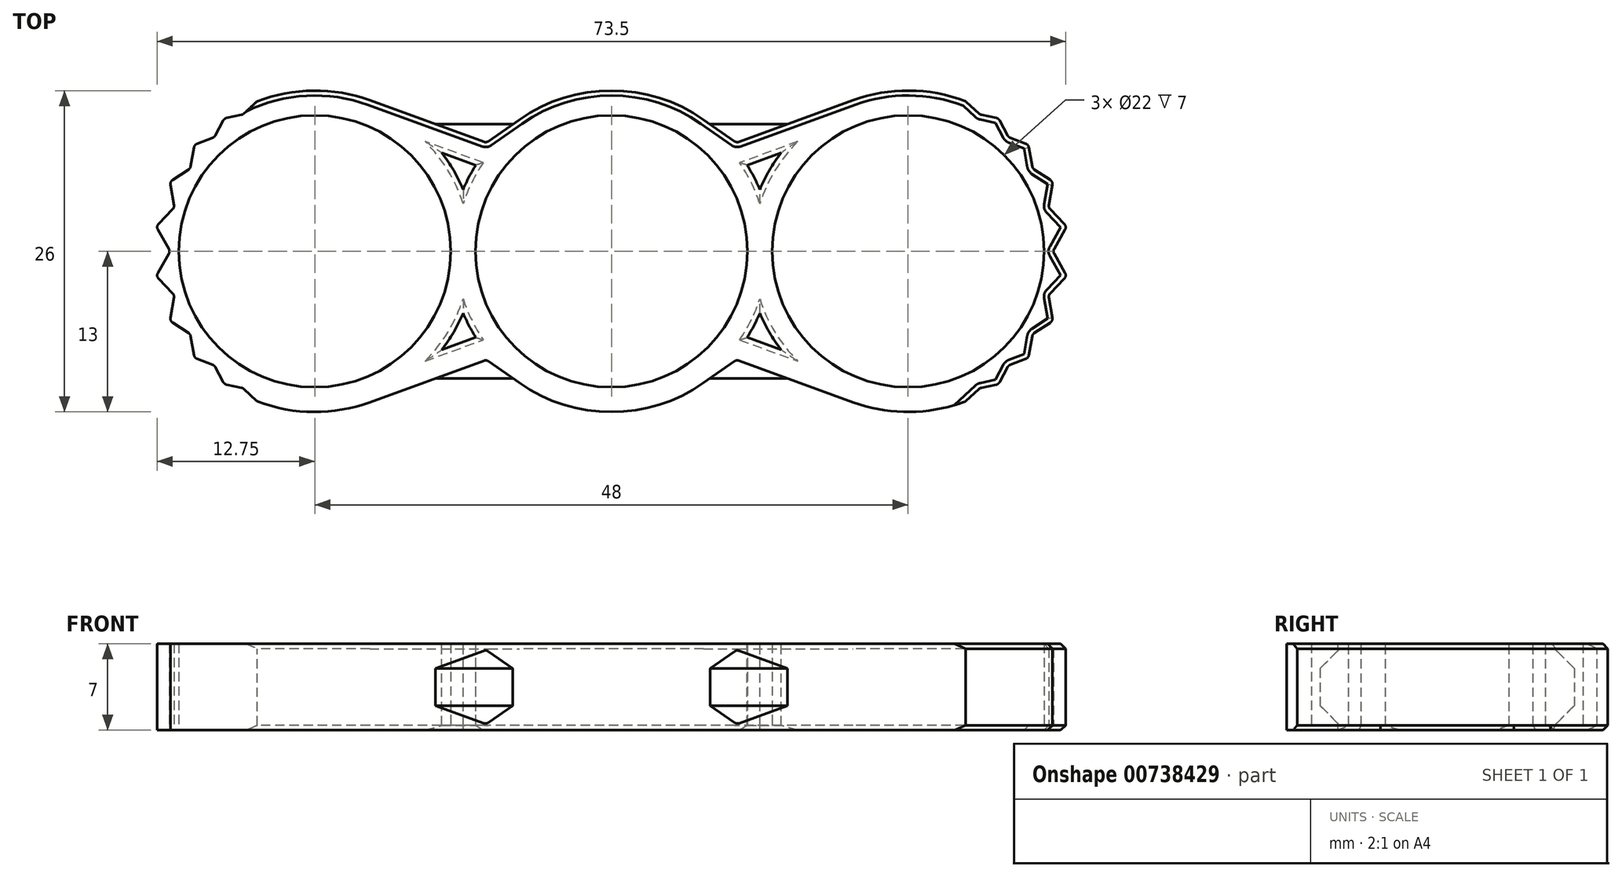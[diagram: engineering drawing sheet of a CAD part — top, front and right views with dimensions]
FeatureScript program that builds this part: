
annotation { "Feature Type Name" : "Feature", "Feature Type Description" : "" }
export const myFeature = defineFeature(function(context is Context, id is Id, definition is map)
    precondition{}
    {
        {
            var Q0;
            Q0=qCreatedBy(makeId("Top.planeOp"),FACE);
            var sketch = newSketch(context, id + "F0", { "sketchPlane" : qUnion([Q0])});
            skCircle(sketch, "E0", {"center": v(0, 0) * mm, "radius": 11 * mm});
            skCircle(sketch, "E1", {"center": v(0, 0) * mm, "radius": 13 * mm});
            skCircle(sketch, "E2", {"center": v(24, 0) * mm, "radius": 11 * mm});
            skCircle(sketch, "E3", {"center": v(-24, 0) * mm, "radius": 11 * mm});
            skLineSegment(sketch, "E4", {"start": v(-24, 0) * mm, "end": v(0, 0) * mm, "construction": true});
            skLineSegment(sketch, "E5", {"start": v(24, 0) * mm, "end": v(0, 0) * mm, "construction": true});
            skCircle(sketch, "E6", {"center": v(24, 0) * mm, "radius": 13 * mm});
            skCircle(sketch, "E7", {"center": v(-24, 0) * mm, "radius": 13 * mm});
            skLineSegment(sketch, "E8", {"start": v(-19.55, 12.22) * mm, "end": v(-10.12, 8.78) * mm});
            skLineSegment(sketch, "E9", {"start": v(-19.55, -12.22) * mm, "end": v(-10.12, -8.78) * mm});
            skLineSegment(sketch, "E10", {"start": v(19.55, -12.22) * mm, "end": v(10.12, -8.78) * mm});
            skLineSegment(sketch, "E11", {"start": v(19.55, 12.22) * mm, "end": v(10.12, 8.78) * mm});
            skLineSegment(sketch, "E12", {"start": v(-10.12, 8.78) * mm, "end": v(-7.46, 10.65) * mm});
            skLineSegment(sketch, "E13", {"start": v(7.46, 10.65) * mm, "end": v(10.12, 8.78) * mm});
            skLineSegment(sketch, "E14", {"start": v(10.12, -8.78) * mm, "end": v(7.46, -10.65) * mm});
            skLineSegment(sketch, "E15", {"start": v(-10.12, -8.78) * mm, "end": v(-7.46, -10.65) * mm});
            skLineSegment(sketch, "E16", {"start": v(10.12, 8.78) * mm, "end": v(10.12, -8.78) * mm, "construction": true});
            skLineSegment(sketch, "E17", {"start": v(-10.12, 8.78) * mm, "end": v(-10.12, -8.78) * mm, "construction": true});
            skSolve(sketch);
        }
        {
            var Q0;
            {var subQ4=sQuery(id+"F0.wireOp",EDGE,"E3");Q0=makeQuery(id+"F0.imprint","IMPRINT",FACE,{"disambiguationData":[TD([[makeQuery(id+"F0.imprint","IMPRINT",EDGE,{"derivedFrom":subQ4}),-1.0]])]});}
            var Q1;
            {var subQ3=sQuery(id+"F0.wireOp",EDGE,"E6");var subQ4=sQuery(id+"F0.wireOp",EDGE,"E0");var subQ5=makeQuery(id+"F0.imprint","INTERSECT",VERTEX,{"derivedFrom":[subQ4,subQ3]});Q1=makeQuery(id+"F0.imprint","IMPRINT",FACE,{"disambiguationData":[TD([[makeQuery(id+"F0.imprint","IMPRINT",EDGE,{"disambiguationData":[TD([[subQ5,-1.0]])],"derivedFrom":subQ4}),-1.0]])]});}
            var Q2;
            {var subQ0=sQuery(id+"F0.wireOp",EDGE,"E1");var subQ1=makeQuery(id+"F0.imprint","INTERSECT",VERTEX,{"derivedFrom":[subQ0,sQuery(id+"F0.wireOp",EDGE,"E3")]});Q2=makeQuery(id+"F0.imprint","IMPRINT",FACE,{"disambiguationData":[TD([[makeQuery(id+"F0.imprint","IMPRINT",EDGE,{"disambiguationData":[TD([[subQ1,1.0]])],"derivedFrom":subQ0}),1.0]])]});}
            var Q3;
            {var subQ2=sQuery(id+"F0.wireOp",EDGE,"E6");var subQ7=sQuery(id+"F0.wireOp",EDGE,"E0");var subQ8=makeQuery(id+"F0.imprint","INTERSECT",VERTEX,{"derivedFrom":[subQ7,subQ2]});Q3=makeQuery(id+"F0.imprint","IMPRINT",FACE,{"disambiguationData":[TD([[makeQuery(id+"F0.imprint","IMPRINT",EDGE,{"disambiguationData":[TD([[subQ8,1.0]])],"derivedFrom":subQ7}),-1.0]])]});}
            var Q4;
            {var subQ0=sQuery(id+"F0.wireOp",EDGE,"E1");var subQ1=makeQuery(id+"F0.imprint","INTERSECT",VERTEX,{"derivedFrom":[subQ0,sQuery(id+"F0.wireOp",EDGE,"E2")]});Q4=makeQuery(id+"F0.imprint","IMPRINT",FACE,{"disambiguationData":[TD([[makeQuery(id+"F0.imprint","IMPRINT",EDGE,{"disambiguationData":[TD([[subQ1,-1.0]])],"derivedFrom":subQ0}),1.0]])]});}
            var Q5;
            {var subQ4=sQuery(id+"F0.wireOp",EDGE,"E2");Q5=makeQuery(id+"F0.imprint","IMPRINT",FACE,{"disambiguationData":[TD([[makeQuery(id+"F0.imprint","IMPRINT",EDGE,{"derivedFrom":subQ4}),-1.0]])]});}
            var Q6;
            {var subQ4=sQuery(id+"F0.wireOp",EDGE,"E8");Q6=makeQuery(id+"F0.imprint","IMPRINT",FACE,{"disambiguationData":[TD([[makeQuery(id+"F0.imprint","IMPRINT",EDGE,{"derivedFrom":subQ4}),-1.0]])]});}
            var Q7;
            {var subQ4=sQuery(id+"F0.wireOp",EDGE,"E11");Q7=makeQuery(id+"F0.imprint","IMPRINT",FACE,{"disambiguationData":[TD([[makeQuery(id+"F0.imprint","IMPRINT",EDGE,{"derivedFrom":subQ4}),1.0]])]});}
            var Q8;
            {var subQ4=sQuery(id+"F0.wireOp",EDGE,"E9");Q8=makeQuery(id+"F0.imprint","IMPRINT",FACE,{"disambiguationData":[TD([[makeQuery(id+"F0.imprint","IMPRINT",EDGE,{"derivedFrom":subQ4}),1.0]])]});}
            var Q9;
            {var subQ4=sQuery(id+"F0.wireOp",EDGE,"E10");Q9=makeQuery(id+"F0.imprint","IMPRINT",FACE,{"disambiguationData":[TD([[makeQuery(id+"F0.imprint","IMPRINT",EDGE,{"derivedFrom":subQ4}),-1.0]])]});}
            extrude(context, id + "F1", {"entities" : qUnion([Q0, Q1, Q2, Q3, Q4, Q5, Q6, Q7, Q8, Q9]), "depth" : 3.5 * mm, "offsetDistance" : 25 * mm, "hasSecondDirection" : true, "secondDirectionOppositeDirection" : true, "secondDirectionDepth" : 3.5 * mm});
        }
        {
            var Q0;
            Q0=qCreatedBy(makeId("Top.planeOp"),FACE);
            var sketch = newSketch(context, id + "F2", { "sketchPlane" : qUnion([Q0])});
            skLineSegment(sketch, "E18", {"start": v(-14.24, -10.28) * mm, "end": v(-10.12, -8.78) * mm});
            skLineSegment(sketch, "E19", {"start": v(-10.12, -8.78) * mm, "end": v(-7.98, -10.28) * mm});
            skLineSegment(sketch, "E20", {"start": v(-7.98, -10.28) * mm, "end": v(-14.24, -10.28) * mm});
            skLineSegment(sketch, "E21", {"start": v(7.98, -10.28) * mm, "end": v(10.12, -8.78) * mm});
            skLineSegment(sketch, "E22", {"start": v(10.12, -8.78) * mm, "end": v(14.24, -10.28) * mm});
            skLineSegment(sketch, "E23", {"start": v(14.24, -10.28) * mm, "end": v(7.98, -10.28) * mm});
            skLineSegment(sketch, "E24", {"start": v(14.24, 10.28) * mm, "end": v(7.98, 10.28) * mm});
            skLineSegment(sketch, "E25", {"start": v(7.98, 10.28) * mm, "end": v(10.12, 8.78) * mm});
            skLineSegment(sketch, "E26", {"start": v(10.12, 8.78) * mm, "end": v(14.24, 10.28) * mm});
            skLineSegment(sketch, "E27", {"start": v(-7.98, 10.28) * mm, "end": v(-14.24, 10.28) * mm});
            skLineSegment(sketch, "E28", {"start": v(-14.24, 10.28) * mm, "end": v(-10.12, 8.78) * mm});
            skLineSegment(sketch, "E29", {"start": v(-10.12, 8.78) * mm, "end": v(-7.98, 10.28) * mm});
            skSolve(sketch);
        }
        {
            var Q0;
            Q0 = qSketchRegion(id + "F2", true);
            extrude(context, id + "F3", {"entities" : qUnion([Q0]), "operationType" : NewBodyOperationType.ADD, "depth" : 3 * mm, "offsetDistance" : 25 * mm, "hasSecondDirection" : true, "secondDirectionOppositeDirection" : true, "secondDirectionDepth" : 3 * mm});
        }
        {
            var Q0;
            Q0=makeQuery(id+"F3.opExtrude","CAP_EDGE",EDGE,{"disambiguationData":[OSD([sQuery(id+"F2.wireOp",EDGE,"E20")])],"isStart":false});
            var Q1;
            Q1=makeQuery(id+"F3.opExtrude","CAP_EDGE",EDGE,{"disambiguationData":[OSD([sQuery(id+"F2.wireOp",EDGE,"E20")])],"isStart":true});
            var Q2;
            Q2=makeQuery(id+"F3.opExtrude","CAP_EDGE",EDGE,{"disambiguationData":[OSD([sQuery(id+"F2.wireOp",EDGE,"E23")])],"isStart":true});
            var Q3;
            Q3=makeQuery(id+"F3.opExtrude","CAP_EDGE",EDGE,{"disambiguationData":[OSD([sQuery(id+"F2.wireOp",EDGE,"E23")])],"isStart":false});
            var Q4;
            Q4=makeQuery(id+"F3.opExtrude","CAP_EDGE",EDGE,{"disambiguationData":[OSD([sQuery(id+"F2.wireOp",EDGE,"E24")])],"isStart":false});
            var Q5;
            Q5=makeQuery(id+"F3.opExtrude","CAP_EDGE",EDGE,{"disambiguationData":[OSD([sQuery(id+"F2.wireOp",EDGE,"E27")])],"isStart":false});
            var Q6;
            Q6=makeQuery(id+"F3.opExtrude","CAP_EDGE",EDGE,{"disambiguationData":[OSD([sQuery(id+"F2.wireOp",EDGE,"E24")])],"isStart":true});
            var Q7;
            Q7=makeQuery(id+"F3.opExtrude","CAP_EDGE",EDGE,{"disambiguationData":[OSD([sQuery(id+"F2.wireOp",EDGE,"E27")])],"isStart":true});
            chamfer(context, id + "F4", {"entities" : qUnion([Q0, Q1, Q2, Q3, Q4, Q5, Q6, Q7]), "width" : 1.5 * mm, "tangentPropagation" : true});
        }
        {
            var Q0;
            Q0=qCreatedBy(makeId("Top.planeOp"),FACE);
            var sketch = newSketch(context, id + "F5", { "sketchPlane" : qUnion([Q0])});
            skLineSegment(sketch, "E30", {"start": v(35.7, 0) * mm, "end": v(36.85, 2) * mm});
            skLineSegment(sketch, "E31", {"start": v(36.85, -2) * mm, "end": v(35.7, 0) * mm});
            skLineSegment(sketch, "E32", {"start": v(35.7, 0) * mm, "end": v(24, 0) * mm, "construction": true});
            skLineSegment(sketch, "E33", {"start": v(36.85, 2) * mm, "end": v(35.36, 3.53) * mm});
            skLineSegment(sketch, "E34", {"start": v(35.36, 3.53) * mm, "end": v(35.72, 5.63) * mm});
            skLineSegment(sketch, "E35", {"start": v(35.36, 3.53) * mm, "end": v(24, 0) * mm, "construction": true});
            skLineSegment(sketch, "E36", {"start": v(35.72, 5.63) * mm, "end": v(34.08, 6.7) * mm});
            skLineSegment(sketch, "E37", {"start": v(34.08, 6.7) * mm, "end": v(33.73, 8.63) * mm});
            skLineSegment(sketch, "E38", {"start": v(34.08, 6.7) * mm, "end": v(24, 0) * mm, "construction": true});
            skLineSegment(sketch, "E39.MirrorCS", {"start": v(36.85, -2) * mm, "end": v(35.36, -3.53) * mm});
            skLineSegment(sketch, "E40.MirrorCS", {"start": v(35.36, -3.53) * mm, "end": v(24, 0) * mm, "construction": true});
            skLineSegment(sketch, "E41.MirrorCS", {"start": v(35.36, -3.53) * mm, "end": v(35.72, -5.63) * mm});
            skLineSegment(sketch, "E42.MirrorCS", {"start": v(35.72, -5.63) * mm, "end": v(34.08, -6.7) * mm});
            skLineSegment(sketch, "E43.MirrorCS", {"start": v(34.08, -6.7) * mm, "end": v(24, 0) * mm, "construction": true});
            skLineSegment(sketch, "E44.MirrorCS", {"start": v(34.08, -6.7) * mm, "end": v(33.73, -8.63) * mm});
            skLineSegment(sketch, "E45", {"start": v(39.5, 12.13) * mm, "end": v(39.5, -12.13) * mm});
            skLineSegment(sketch, "E46", {"start": v(33.73, 8.63) * mm, "end": v(32.13, 9.23) * mm});
            skLineSegment(sketch, "E47", {"start": v(32.13, 9.23) * mm, "end": v(31.32, 10.74) * mm});
            skLineSegment(sketch, "E48", {"start": v(32.13, 9.23) * mm, "end": v(24, 0) * mm, "construction": true});
            skLineSegment(sketch, "E49.MirrorCS", {"start": v(32.13, -9.23) * mm, "end": v(24, 0) * mm, "construction": true});
            skLineSegment(sketch, "E50.MirrorCS", {"start": v(32.13, -9.23) * mm, "end": v(31.32, -10.74) * mm});
            skLineSegment(sketch, "E51.MirrorCS", {"start": v(33.73, -8.63) * mm, "end": v(32.13, -9.23) * mm});
            skLineSegment(sketch, "E52", {"start": v(31.32, 10.74) * mm, "end": v(29.8, 11.07) * mm});
            skLineSegment(sketch, "E53", {"start": v(29.8, 11.07) * mm, "end": v(28.67, 12.13) * mm});
            skLineSegment(sketch, "E54", {"start": v(29.8, 11.07) * mm, "end": v(24, 0) * mm, "construction": true});
            skLineSegment(sketch, "E55", {"start": v(28.67, 12.13) * mm, "end": v(39.5, 12.13) * mm});
            skLineSegment(sketch, "E56.MirrorCS", {"start": v(29.8, -11.07) * mm, "end": v(24, 0) * mm, "construction": true});
            skLineSegment(sketch, "E57.MirrorCS", {"start": v(31.32, -10.74) * mm, "end": v(29.8, -11.07) * mm});
            skLineSegment(sketch, "E58.MirrorCS", {"start": v(29.8, -11.07) * mm, "end": v(28.67, -12.13) * mm});
            skLineSegment(sketch, "E59", {"start": v(28.67, -12.13) * mm, "end": v(39.5, -12.13) * mm});
            skLineSegment(sketch, "E60", {"start": v(0, 0) * mm, "end": v(0, 11) * mm, "construction": true});
            skLineSegment(sketch, "E61.MirrorCS", {"start": v(-29.8, 11.07) * mm, "end": v(-28.67, 12.13) * mm});
            skLineSegment(sketch, "E62.MirrorCS", {"start": v(-29.8, -11.07) * mm, "end": v(-28.67, -12.13) * mm});
            skLineSegment(sketch, "E63.MirrorCS", {"start": v(-31.32, -10.74) * mm, "end": v(-29.8, -11.07) * mm});
            skLineSegment(sketch, "E64.MirrorCS", {"start": v(-32.13, -9.23) * mm, "end": v(-31.32, -10.74) * mm});
            skLineSegment(sketch, "E65.MirrorCS", {"start": v(-31.32, 10.74) * mm, "end": v(-29.8, 11.07) * mm});
            skLineSegment(sketch, "E66.MirrorCS", {"start": v(-34.08, 6.7) * mm, "end": v(-33.73, 8.63) * mm});
            skLineSegment(sketch, "E67.MirrorCS", {"start": v(-34.08, -6.7) * mm, "end": v(-33.73, -8.63) * mm});
            skLineSegment(sketch, "E68.MirrorCS", {"start": v(-35.72, 5.63) * mm, "end": v(-34.08, 6.7) * mm});
            skLineSegment(sketch, "E69.MirrorCS", {"start": v(-33.73, 8.63) * mm, "end": v(-32.13, 9.23) * mm});
            skLineSegment(sketch, "E70.MirrorCS", {"start": v(-32.13, 9.23) * mm, "end": v(-31.32, 10.74) * mm});
            skLineSegment(sketch, "E71.MirrorCS", {"start": v(-33.73, -8.63) * mm, "end": v(-32.13, -9.23) * mm});
            skLineSegment(sketch, "E72.MirrorCS", {"start": v(-36.85, 2) * mm, "end": v(-35.36, 3.53) * mm});
            skLineSegment(sketch, "E73.MirrorCS", {"start": v(-35.72, -5.63) * mm, "end": v(-34.08, -6.7) * mm});
            skLineSegment(sketch, "E74.MirrorCS", {"start": v(-36.85, -2) * mm, "end": v(-35.7, 0) * mm});
            skLineSegment(sketch, "E75.MirrorCS", {"start": v(-32.13, 9.23) * mm, "end": v(-24, 0) * mm, "construction": true});
            skLineSegment(sketch, "E76.MirrorCS", {"start": v(-35.7, 0) * mm, "end": v(-36.85, 2) * mm});
            skLineSegment(sketch, "E77.MirrorCS", {"start": v(-35.36, -3.53) * mm, "end": v(-35.72, -5.63) * mm});
            skLineSegment(sketch, "E78.MirrorCS", {"start": v(-28.67, 12.13) * mm, "end": v(-39.5, 12.13) * mm});
            skLineSegment(sketch, "E79.MirrorCS", {"start": v(-34.08, -6.7) * mm, "end": v(-24, 0) * mm, "construction": true});
            skLineSegment(sketch, "E80.MirrorCS", {"start": v(-29.8, -11.07) * mm, "end": v(-24, 0) * mm, "construction": true});
            skLineSegment(sketch, "E81.MirrorCS", {"start": v(-36.85, -2) * mm, "end": v(-35.36, -3.53) * mm});
            skLineSegment(sketch, "E82.MirrorCS", {"start": v(-35.36, 3.53) * mm, "end": v(-24, 0) * mm, "construction": true});
            skLineSegment(sketch, "E83.MirrorCS", {"start": v(-35.7, 0) * mm, "end": v(-24, 0) * mm, "construction": true});
            skLineSegment(sketch, "E84.MirrorCS", {"start": v(-35.36, 3.53) * mm, "end": v(-35.72, 5.63) * mm});
            skLineSegment(sketch, "E85.MirrorCS", {"start": v(-28.67, -12.13) * mm, "end": v(-39.5, -12.13) * mm});
            skLineSegment(sketch, "E86.MirrorCS", {"start": v(-29.8, 11.07) * mm, "end": v(-24, 0) * mm, "construction": true});
            skLineSegment(sketch, "E87.MirrorCS", {"start": v(-34.08, 6.7) * mm, "end": v(-24, 0) * mm, "construction": true});
            skLineSegment(sketch, "E88.MirrorCS", {"start": v(-32.13, -9.23) * mm, "end": v(-24, 0) * mm, "construction": true});
            skLineSegment(sketch, "E89.MirrorCS", {"start": v(-35.36, -3.53) * mm, "end": v(-24, 0) * mm, "construction": true});
            skLineSegment(sketch, "E90.MirrorCS", {"start": v(-39.5, 12.13) * mm, "end": v(-39.5, -12.13) * mm});
            skSolve(sketch);
        }
        {
            var Q0;
            Q0 = qSketchRegion(id + "F5", true);
            extrude(context, id + "F6", {"entities" : qUnion([Q0]), "operationType" : NewBodyOperationType.REMOVE, "endBound" : BoundingType.THROUGH_ALL, "oppositeDirection" : true, "depth" : 25 * mm, "offsetDistance" : 25 * mm, "hasSecondDirection" : true, "secondDirectionBound" : SecondDirectionBoundingType.THROUGH_ALL, "secondDirectionOppositeDirection" : false, "secondDirectionDepth" : 25 * mm});
        }
        {
            var Q0;
            Q0=makeQuery(id+"F6.boolean.opBoolean","COPY",EDGE,{"derivedFrom":makeQuery(id+"F6.opExtrude","SWEPT_EDGE",EDGE,{"disambiguationData":[OSD([sQuery(id+"F5.wireOp",EDGE,"E61.MirrorCS"),sQuery(id+"F5.wireOp",EDGE,"E78.MirrorCS")])]})});
            var Q1;
            Q1=makeQuery(id+"F6.boolean.opBoolean","COPY",EDGE,{"derivedFrom":makeQuery(id+"F6.opExtrude","SWEPT_EDGE",EDGE,{"disambiguationData":[OSD([sQuery(id+"F5.wireOp",EDGE,"E61.MirrorCS"),sQuery(id+"F5.wireOp",EDGE,"E65.MirrorCS")])]})});
            var Q2;
            Q2=makeQuery(id+"F6.boolean.opBoolean","COPY",EDGE,{"derivedFrom":makeQuery(id+"F6.opExtrude","SWEPT_EDGE",EDGE,{"disambiguationData":[OSD([sQuery(id+"F5.wireOp",EDGE,"E65.MirrorCS"),sQuery(id+"F5.wireOp",EDGE,"E70.MirrorCS")])]})});
            var Q3;
            Q3=makeQuery(id+"F6.boolean.opBoolean","COPY",EDGE,{"derivedFrom":makeQuery(id+"F6.opExtrude","SWEPT_EDGE",EDGE,{"disambiguationData":[OSD([sQuery(id+"F5.wireOp",EDGE,"E69.MirrorCS"),sQuery(id+"F5.wireOp",EDGE,"E70.MirrorCS")])]})});
            var Q4;
            Q4=makeQuery(id+"F6.boolean.opBoolean","COPY",EDGE,{"derivedFrom":makeQuery(id+"F6.opExtrude","SWEPT_EDGE",EDGE,{"disambiguationData":[OSD([sQuery(id+"F5.wireOp",EDGE,"E66.MirrorCS"),sQuery(id+"F5.wireOp",EDGE,"E69.MirrorCS")])]})});
            var Q5;
            Q5=makeQuery(id+"F6.boolean.opBoolean","COPY",EDGE,{"derivedFrom":makeQuery(id+"F6.opExtrude","SWEPT_EDGE",EDGE,{"disambiguationData":[OSD([sQuery(id+"F5.wireOp",EDGE,"E66.MirrorCS"),sQuery(id+"F5.wireOp",EDGE,"E68.MirrorCS")])]})});
            var Q6;
            Q6=makeQuery(id+"F6.boolean.opBoolean","COPY",EDGE,{"derivedFrom":makeQuery(id+"F6.opExtrude","SWEPT_EDGE",EDGE,{"disambiguationData":[OSD([sQuery(id+"F5.wireOp",EDGE,"E68.MirrorCS"),sQuery(id+"F5.wireOp",EDGE,"E84.MirrorCS")])]})});
            var Q7;
            Q7=makeQuery(id+"F6.boolean.opBoolean","COPY",EDGE,{"derivedFrom":makeQuery(id+"F6.opExtrude","SWEPT_EDGE",EDGE,{"disambiguationData":[OSD([sQuery(id+"F5.wireOp",EDGE,"E72.MirrorCS"),sQuery(id+"F5.wireOp",EDGE,"E84.MirrorCS")])]})});
            var Q8;
            Q8=makeQuery(id+"F6.boolean.opBoolean","COPY",EDGE,{"derivedFrom":makeQuery(id+"F6.opExtrude","SWEPT_EDGE",EDGE,{"disambiguationData":[OSD([sQuery(id+"F5.wireOp",EDGE,"E72.MirrorCS"),sQuery(id+"F5.wireOp",EDGE,"E76.MirrorCS")])]})});
            var Q9;
            Q9=makeQuery(id+"F6.boolean.opBoolean","COPY",EDGE,{"derivedFrom":makeQuery(id+"F6.opExtrude","SWEPT_EDGE",EDGE,{"disambiguationData":[OSD([sQuery(id+"F5.wireOp",EDGE,"E74.MirrorCS"),sQuery(id+"F5.wireOp",EDGE,"E76.MirrorCS")])]})});
            var Q10;
            Q10=makeQuery(id+"F6.boolean.opBoolean","COPY",EDGE,{"derivedFrom":makeQuery(id+"F6.opExtrude","SWEPT_EDGE",EDGE,{"disambiguationData":[OSD([sQuery(id+"F5.wireOp",EDGE,"E74.MirrorCS"),sQuery(id+"F5.wireOp",EDGE,"E81.MirrorCS")])]})});
            var Q11;
            Q11=makeQuery(id+"F6.boolean.opBoolean","COPY",EDGE,{"derivedFrom":makeQuery(id+"F6.opExtrude","SWEPT_EDGE",EDGE,{"disambiguationData":[OSD([sQuery(id+"F5.wireOp",EDGE,"E77.MirrorCS"),sQuery(id+"F5.wireOp",EDGE,"E81.MirrorCS")])]})});
            var Q12;
            Q12=makeQuery(id+"F6.boolean.opBoolean","COPY",EDGE,{"derivedFrom":makeQuery(id+"F6.opExtrude","SWEPT_EDGE",EDGE,{"disambiguationData":[OSD([sQuery(id+"F5.wireOp",EDGE,"E73.MirrorCS"),sQuery(id+"F5.wireOp",EDGE,"E77.MirrorCS")])]})});
            var Q13;
            Q13=makeQuery(id+"F6.boolean.opBoolean","COPY",EDGE,{"derivedFrom":makeQuery(id+"F6.opExtrude","SWEPT_EDGE",EDGE,{"disambiguationData":[OSD([sQuery(id+"F5.wireOp",EDGE,"E67.MirrorCS"),sQuery(id+"F5.wireOp",EDGE,"E73.MirrorCS")])]})});
            var Q14;
            Q14=makeQuery(id+"F6.boolean.opBoolean","COPY",EDGE,{"derivedFrom":makeQuery(id+"F6.opExtrude","SWEPT_EDGE",EDGE,{"disambiguationData":[OSD([sQuery(id+"F5.wireOp",EDGE,"E67.MirrorCS"),sQuery(id+"F5.wireOp",EDGE,"E71.MirrorCS")])]})});
            var Q15;
            Q15=makeQuery(id+"F6.boolean.opBoolean","COPY",EDGE,{"derivedFrom":makeQuery(id+"F6.opExtrude","SWEPT_EDGE",EDGE,{"disambiguationData":[OSD([sQuery(id+"F5.wireOp",EDGE,"E64.MirrorCS"),sQuery(id+"F5.wireOp",EDGE,"E71.MirrorCS")])]})});
            var Q16;
            Q16=makeQuery(id+"F6.boolean.opBoolean","COPY",EDGE,{"derivedFrom":makeQuery(id+"F6.opExtrude","SWEPT_EDGE",EDGE,{"disambiguationData":[OSD([sQuery(id+"F5.wireOp",EDGE,"E63.MirrorCS"),sQuery(id+"F5.wireOp",EDGE,"E64.MirrorCS")])]})});
            var Q17;
            Q17=makeQuery(id+"F6.boolean.opBoolean","COPY",EDGE,{"derivedFrom":makeQuery(id+"F6.opExtrude","SWEPT_EDGE",EDGE,{"disambiguationData":[OSD([sQuery(id+"F5.wireOp",EDGE,"E62.MirrorCS"),sQuery(id+"F5.wireOp",EDGE,"E63.MirrorCS")])]})});
            var Q18;
            Q18=makeQuery(id+"F6.boolean.opBoolean","COPY",EDGE,{"derivedFrom":makeQuery(id+"F6.opExtrude","SWEPT_EDGE",EDGE,{"disambiguationData":[OSD([sQuery(id+"F5.wireOp",EDGE,"E62.MirrorCS"),sQuery(id+"F5.wireOp",EDGE,"E85.MirrorCS")])]})});
            var Q19;
            Q19=makeQuery(id+"F6.boolean.opBoolean","COPY",EDGE,{"derivedFrom":makeQuery(id+"F6.opExtrude","SWEPT_EDGE",EDGE,{"disambiguationData":[OSD([sQuery(id+"F5.wireOp",EDGE,"E58.MirrorCS"),sQuery(id+"F5.wireOp",EDGE,"E59")])]})});
            var Q20;
            Q20=makeQuery(id+"F6.boolean.opBoolean","COPY",EDGE,{"derivedFrom":makeQuery(id+"F6.opExtrude","SWEPT_EDGE",EDGE,{"disambiguationData":[OSD([sQuery(id+"F5.wireOp",EDGE,"E57.MirrorCS"),sQuery(id+"F5.wireOp",EDGE,"E58.MirrorCS")])]})});
            var Q21;
            Q21=makeQuery(id+"F6.boolean.opBoolean","COPY",EDGE,{"derivedFrom":makeQuery(id+"F6.opExtrude","SWEPT_EDGE",EDGE,{"disambiguationData":[OSD([sQuery(id+"F5.wireOp",EDGE,"E50.MirrorCS"),sQuery(id+"F5.wireOp",EDGE,"E57.MirrorCS")])]})});
            var Q22;
            Q22=makeQuery(id+"F6.boolean.opBoolean","COPY",EDGE,{"derivedFrom":makeQuery(id+"F6.opExtrude","SWEPT_EDGE",EDGE,{"disambiguationData":[OSD([sQuery(id+"F5.wireOp",EDGE,"E50.MirrorCS"),sQuery(id+"F5.wireOp",EDGE,"E51.MirrorCS")])]})});
            var Q23;
            Q23=makeQuery(id+"F6.boolean.opBoolean","COPY",EDGE,{"derivedFrom":makeQuery(id+"F6.opExtrude","SWEPT_EDGE",EDGE,{"disambiguationData":[OSD([sQuery(id+"F5.wireOp",EDGE,"E44.MirrorCS"),sQuery(id+"F5.wireOp",EDGE,"E51.MirrorCS")])]})});
            var Q24;
            Q24=makeQuery(id+"F6.boolean.opBoolean","COPY",EDGE,{"derivedFrom":makeQuery(id+"F6.opExtrude","SWEPT_EDGE",EDGE,{"disambiguationData":[OSD([sQuery(id+"F5.wireOp",EDGE,"E42.MirrorCS"),sQuery(id+"F5.wireOp",EDGE,"E44.MirrorCS")])]})});
            var Q25;
            Q25=makeQuery(id+"F6.boolean.opBoolean","COPY",EDGE,{"derivedFrom":makeQuery(id+"F6.opExtrude","SWEPT_EDGE",EDGE,{"disambiguationData":[OSD([sQuery(id+"F5.wireOp",EDGE,"E41.MirrorCS"),sQuery(id+"F5.wireOp",EDGE,"E42.MirrorCS")])]})});
            var Q26;
            Q26=makeQuery(id+"F6.boolean.opBoolean","COPY",EDGE,{"derivedFrom":makeQuery(id+"F6.opExtrude","SWEPT_EDGE",EDGE,{"disambiguationData":[OSD([sQuery(id+"F5.wireOp",EDGE,"E39.MirrorCS"),sQuery(id+"F5.wireOp",EDGE,"E41.MirrorCS")])]})});
            var Q27;
            Q27=makeQuery(id+"F6.boolean.opBoolean","COPY",EDGE,{"derivedFrom":makeQuery(id+"F6.opExtrude","SWEPT_EDGE",EDGE,{"disambiguationData":[OSD([sQuery(id+"F5.wireOp",EDGE,"E31"),sQuery(id+"F5.wireOp",EDGE,"E39.MirrorCS")])]})});
            var Q28;
            Q28=makeQuery(id+"F6.boolean.opBoolean","COPY",EDGE,{"derivedFrom":makeQuery(id+"F6.opExtrude","SWEPT_EDGE",EDGE,{"disambiguationData":[OSD([sQuery(id+"F5.wireOp",EDGE,"E30"),sQuery(id+"F5.wireOp",EDGE,"E31")])]})});
            var Q29;
            Q29=makeQuery(id+"F6.boolean.opBoolean","COPY",EDGE,{"derivedFrom":makeQuery(id+"F6.opExtrude","SWEPT_EDGE",EDGE,{"disambiguationData":[OSD([sQuery(id+"F5.wireOp",EDGE,"E30"),sQuery(id+"F5.wireOp",EDGE,"E33")])]})});
            var Q30;
            Q30=makeQuery(id+"F6.boolean.opBoolean","COPY",EDGE,{"derivedFrom":makeQuery(id+"F6.opExtrude","SWEPT_EDGE",EDGE,{"disambiguationData":[OSD([sQuery(id+"F5.wireOp",EDGE,"E33"),sQuery(id+"F5.wireOp",EDGE,"E34")])]})});
            var Q31;
            Q31=makeQuery(id+"F6.boolean.opBoolean","COPY",EDGE,{"derivedFrom":makeQuery(id+"F6.opExtrude","SWEPT_EDGE",EDGE,{"disambiguationData":[OSD([sQuery(id+"F5.wireOp",EDGE,"E34"),sQuery(id+"F5.wireOp",EDGE,"E36")])]})});
            var Q32;
            Q32=makeQuery(id+"F6.boolean.opBoolean","COPY",EDGE,{"derivedFrom":makeQuery(id+"F6.opExtrude","SWEPT_EDGE",EDGE,{"disambiguationData":[OSD([sQuery(id+"F5.wireOp",EDGE,"E36"),sQuery(id+"F5.wireOp",EDGE,"E37")])]})});
            var Q33;
            Q33=makeQuery(id+"F6.boolean.opBoolean","COPY",EDGE,{"derivedFrom":makeQuery(id+"F6.opExtrude","SWEPT_EDGE",EDGE,{"disambiguationData":[OSD([sQuery(id+"F5.wireOp",EDGE,"E37"),sQuery(id+"F5.wireOp",EDGE,"E46")])]})});
            var Q34;
            Q34=makeQuery(id+"F6.boolean.opBoolean","COPY",EDGE,{"derivedFrom":makeQuery(id+"F6.opExtrude","SWEPT_EDGE",EDGE,{"disambiguationData":[OSD([sQuery(id+"F5.wireOp",EDGE,"E46"),sQuery(id+"F5.wireOp",EDGE,"E47")])]})});
            var Q35;
            Q35=makeQuery(id+"F6.boolean.opBoolean","COPY",EDGE,{"derivedFrom":makeQuery(id+"F6.opExtrude","SWEPT_EDGE",EDGE,{"disambiguationData":[OSD([sQuery(id+"F5.wireOp",EDGE,"E47"),sQuery(id+"F5.wireOp",EDGE,"E52")])]})});
            var Q36;
            Q36=makeQuery(id+"F6.boolean.opBoolean","COPY",EDGE,{"derivedFrom":makeQuery(id+"F6.opExtrude","SWEPT_EDGE",EDGE,{"disambiguationData":[OSD([sQuery(id+"F5.wireOp",EDGE,"E52"),sQuery(id+"F5.wireOp",EDGE,"E53")])]})});
            var Q37;
            Q37=makeQuery(id+"F6.boolean.opBoolean","COPY",EDGE,{"derivedFrom":makeQuery(id+"F6.opExtrude","SWEPT_EDGE",EDGE,{"disambiguationData":[OSD([sQuery(id+"F5.wireOp",EDGE,"E53"),sQuery(id+"F5.wireOp",EDGE,"E55")])]})});
            var Q38;
            {var subQ0=sQuery(id+"F0.wireOp",EDGE,"E13");var subQ1=sQuery(id+"F0.wireOp",EDGE,"E11");Q38=makeQuery(id+"F3.boolean.opBoolean","SPLIT",EDGE,{"disambiguationData":[TD([makeQuery(id+"F3.opExtrude","CAP_FACE",FACE,{"disambiguationData":[OSD([sQuery(id+"F2.wireOp",EDGE,"E24"),sQuery(id+"F2.wireOp",EDGE,"E25"),sQuery(id+"F2.wireOp",EDGE,"E26")])],"isStart":false})])],"derivedFrom":makeQuery(id+"F1.opExtrude","SWEPT_EDGE",EDGE,{"disambiguationData":[OSD([subQ1,subQ0])]})});}
            var Q39;
            {var subQ0=sQuery(id+"F0.wireOp",EDGE,"E13");var subQ1=sQuery(id+"F0.wireOp",EDGE,"E11");Q39=makeQuery(id+"F3.boolean.opBoolean","SPLIT",EDGE,{"disambiguationData":[TD([makeQuery(id+"F3.opExtrude","CAP_FACE",FACE,{"disambiguationData":[OSD([sQuery(id+"F2.wireOp",EDGE,"E24"),sQuery(id+"F2.wireOp",EDGE,"E25"),sQuery(id+"F2.wireOp",EDGE,"E26")])],"isStart":true})])],"derivedFrom":makeQuery(id+"F1.opExtrude","SWEPT_EDGE",EDGE,{"disambiguationData":[OSD([subQ1,subQ0])]})});}
            var Q40;
            {var subQ0=sQuery(id+"F0.wireOp",EDGE,"E12");var subQ1=sQuery(id+"F0.wireOp",EDGE,"E8");Q40=makeQuery(id+"F3.boolean.opBoolean","SPLIT",EDGE,{"disambiguationData":[TD([makeQuery(id+"F3.opExtrude","CAP_FACE",FACE,{"disambiguationData":[OSD([sQuery(id+"F2.wireOp",EDGE,"E27"),sQuery(id+"F2.wireOp",EDGE,"E28"),sQuery(id+"F2.wireOp",EDGE,"E29")])],"isStart":false})])],"derivedFrom":makeQuery(id+"F1.opExtrude","SWEPT_EDGE",EDGE,{"disambiguationData":[OSD([subQ1,subQ0])]})});}
            var Q41;
            {var subQ0=sQuery(id+"F0.wireOp",EDGE,"E12");var subQ1=sQuery(id+"F0.wireOp",EDGE,"E8");Q41=makeQuery(id+"F3.boolean.opBoolean","SPLIT",EDGE,{"disambiguationData":[TD([makeQuery(id+"F3.opExtrude","CAP_FACE",FACE,{"disambiguationData":[OSD([sQuery(id+"F2.wireOp",EDGE,"E27"),sQuery(id+"F2.wireOp",EDGE,"E28"),sQuery(id+"F2.wireOp",EDGE,"E29")])],"isStart":true})])],"derivedFrom":makeQuery(id+"F1.opExtrude","SWEPT_EDGE",EDGE,{"disambiguationData":[OSD([subQ1,subQ0])]})});}
            var Q42;
            {var subQ0=sQuery(id+"F0.wireOp",EDGE,"E15");var subQ1=sQuery(id+"F0.wireOp",EDGE,"E9");Q42=makeQuery(id+"F3.boolean.opBoolean","SPLIT",EDGE,{"disambiguationData":[TD([makeQuery(id+"F3.opExtrude","CAP_FACE",FACE,{"disambiguationData":[OSD([sQuery(id+"F2.wireOp",EDGE,"E18"),sQuery(id+"F2.wireOp",EDGE,"E19"),sQuery(id+"F2.wireOp",EDGE,"E20")])],"isStart":false})])],"derivedFrom":makeQuery(id+"F1.opExtrude","SWEPT_EDGE",EDGE,{"disambiguationData":[OSD([subQ1,subQ0])]})});}
            var Q43;
            {var subQ0=sQuery(id+"F0.wireOp",EDGE,"E15");var subQ1=sQuery(id+"F0.wireOp",EDGE,"E9");Q43=makeQuery(id+"F3.boolean.opBoolean","SPLIT",EDGE,{"disambiguationData":[TD([makeQuery(id+"F3.opExtrude","CAP_FACE",FACE,{"disambiguationData":[OSD([sQuery(id+"F2.wireOp",EDGE,"E18"),sQuery(id+"F2.wireOp",EDGE,"E19"),sQuery(id+"F2.wireOp",EDGE,"E20")])],"isStart":true})])],"derivedFrom":makeQuery(id+"F1.opExtrude","SWEPT_EDGE",EDGE,{"disambiguationData":[OSD([subQ1,subQ0])]})});}
            var Q44;
            {var subQ0=sQuery(id+"F0.wireOp",EDGE,"E14");var subQ1=sQuery(id+"F0.wireOp",EDGE,"E10");Q44=makeQuery(id+"F3.boolean.opBoolean","SPLIT",EDGE,{"disambiguationData":[TD([makeQuery(id+"F3.opExtrude","CAP_FACE",FACE,{"disambiguationData":[OSD([sQuery(id+"F2.wireOp",EDGE,"E21"),sQuery(id+"F2.wireOp",EDGE,"E22"),sQuery(id+"F2.wireOp",EDGE,"E23")])],"isStart":false})])],"derivedFrom":makeQuery(id+"F1.opExtrude","SWEPT_EDGE",EDGE,{"disambiguationData":[OSD([subQ1,subQ0])]})});}
            var Q45;
            {var subQ0=sQuery(id+"F0.wireOp",EDGE,"E14");var subQ1=sQuery(id+"F0.wireOp",EDGE,"E10");Q45=makeQuery(id+"F3.boolean.opBoolean","SPLIT",EDGE,{"disambiguationData":[TD([makeQuery(id+"F3.opExtrude","CAP_FACE",FACE,{"disambiguationData":[OSD([sQuery(id+"F2.wireOp",EDGE,"E21"),sQuery(id+"F2.wireOp",EDGE,"E22"),sQuery(id+"F2.wireOp",EDGE,"E23")])],"isStart":true})])],"derivedFrom":makeQuery(id+"F1.opExtrude","SWEPT_EDGE",EDGE,{"disambiguationData":[OSD([subQ1,subQ0])]})});}
            fillet(context, id + "F7", {"entities" : qUnion([Q0, Q1, Q2, Q3, Q4, Q5, Q6, Q7, Q8, Q9, Q10, Q11, Q12, Q13, Q14, Q15, Q16, Q17, Q18, Q19, Q20, Q21, Q22, Q23, Q24, Q25, Q26, Q27, Q28, Q29, Q30, Q31, Q32, Q33, Q34, Q35, Q36, Q37, Q38, Q39, Q40, Q41, Q42, Q43, Q44, Q45]), "radius" : 0.4 * mm, "tangentPropagation" : true, "allowEdgeOverflow" : false});
        }
        {
            var Q0;
            Q0=makeQuery(id+"F1.opExtrude","CAP_FACE",FACE,{"disambiguationData":[OSD([sQuery(id+"F0.wireOp",EDGE,"E0"),sQuery(id+"F0.wireOp",EDGE,"E1"),sQuery(id+"F0.wireOp",EDGE,"E2"),sQuery(id+"F0.wireOp",EDGE,"E3"),sQuery(id+"F0.wireOp",EDGE,"E6"),sQuery(id+"F0.wireOp",EDGE,"E7"),sQuery(id+"F0.wireOp",EDGE,"E8"),sQuery(id+"F0.wireOp",EDGE,"E9"),sQuery(id+"F0.wireOp",EDGE,"E10"),sQuery(id+"F0.wireOp",EDGE,"E11"),sQuery(id+"F0.wireOp",EDGE,"E12"),sQuery(id+"F0.wireOp",EDGE,"E13"),sQuery(id+"F0.wireOp",EDGE,"E14"),sQuery(id+"F0.wireOp",EDGE,"E15")])],"isStart":false});
            var sketch = newSketch(context, id + "F8", { "sketchPlane" : qUnion([Q0])});
            skCircle(sketch, "E91", {"center": v(0, 0) * mm, "radius": 11 * mm, "construction": true});
            skCircle(sketch, "E92", {"center": v(24, 0) * mm, "radius": 11 * mm, "construction": true});
            skArc(sketch, "E93", {"start": v(10.98, -6.97) * mm, "mid": v(11.53, -6) * mm, "end": v(12, -5) * mm});
            skArc(sketch, "E94", {"start": v(12, -5) * mm, "mid": v(12.77, -6.54) * mm, "end": v(13.73, -7.97) * mm});
            skLineSegment(sketch, "E95", {"start": v(10.98, -6.97) * mm, "end": v(13.73, -7.97) * mm});
            skLineSegment(sketch, "E96", {"start": v(0, 0) * mm, "end": v(11, 0) * mm, "construction": true});
            skLineSegment(sketch, "E97", {"start": v(0, 0) * mm, "end": v(0, 11) * mm, "construction": true});
            skArc(sketch, "E98.MirrorCS", {"start": v(10.98, 6.97) * mm, "mid": v(11.53, 6) * mm, "end": v(12, 5) * mm});
            skLineSegment(sketch, "E99.MirrorCS", {"start": v(10.98, 6.97) * mm, "end": v(13.73, 7.97) * mm});
            skArc(sketch, "E100.MirrorCS", {"start": v(12, 5) * mm, "mid": v(12.77, 6.54) * mm, "end": v(13.73, 7.97) * mm});
            skLineSegment(sketch, "E101.MirrorCS", {"start": v(-10.98, 6.97) * mm, "end": v(-13.73, 7.97) * mm});
            skArc(sketch, "E102.MirrorCS", {"start": v(-10.98, 6.97) * mm, "mid": v(-11.53, 6) * mm, "end": v(-12, 5) * mm});
            skArc(sketch, "E103.MirrorCS", {"start": v(-12, 5) * mm, "mid": v(-12.77, 6.54) * mm, "end": v(-13.73, 7.97) * mm});
            skArc(sketch, "E104.MirrorCS", {"start": v(-10.98, -6.97) * mm, "mid": v(-11.53, -6) * mm, "end": v(-12, -5) * mm});
            skLineSegment(sketch, "E105.MirrorCS", {"start": v(-10.98, -6.97) * mm, "end": v(-13.73, -7.97) * mm});
            skArc(sketch, "E106.MirrorCS", {"start": v(-12, -5) * mm, "mid": v(-12.77, -6.54) * mm, "end": v(-13.73, -7.97) * mm});
            skSolve(sketch);
        }
        {
            var Q0;
            Q0 = qSketchRegion(id + "F8", true);
            extrude(context, id + "F9", {"entities" : qUnion([Q0]), "operationType" : NewBodyOperationType.REMOVE, "endBound" : BoundingType.THROUGH_ALL, "oppositeDirection" : true, "depth" : 25 * mm, "offsetDistance" : 25 * mm});
        }
        {
            var Q0;
            {var subQ0=sQuery(id+"F0.wireOp",EDGE,"E1");Q0=makeQuery(id+"F1.opExtrude","CAP_EDGE",EDGE,{"disambiguationData":[OSD([subQ0]),TDD([makeQuery(id+"F0.imprint","IMPRINT",EDGE,{"disambiguationData":[TD([[makeQuery(id+"F0.imprint","INTERSECT",VERTEX,{"derivedFrom":[subQ0,sQuery(id+"F0.wireOp",EDGE,"E12")]}),1.0]])],"derivedFrom":subQ0})])],"isStart":false});}
            var Q1;
            {var subQ0=sQuery(id+"F0.wireOp",EDGE,"E1");Q1=makeQuery(id+"F1.opExtrude","CAP_EDGE",EDGE,{"disambiguationData":[OSD([subQ0]),TDD([makeQuery(id+"F0.imprint","IMPRINT",EDGE,{"disambiguationData":[TD([[makeQuery(id+"F0.imprint","INTERSECT",VERTEX,{"derivedFrom":[subQ0,sQuery(id+"F0.wireOp",EDGE,"E12")]}),1.0]])],"derivedFrom":subQ0})])],"isStart":true});}
            var Q2;
            Q2=makeQuery(id+"F9.boolean.opBoolean","COPY",EDGE,{"derivedFrom":makeQuery(id+"F9.opExtrude","CAP_EDGE",EDGE,{"disambiguationData":[OSD([sQuery(id+"F8.wireOp",EDGE,"E94")])],"isStart":true})});
            var Q3;
            Q3=makeQuery(id+"F9.boolean.opBoolean","COPY",EDGE,{"derivedFrom":makeQuery(id+"F9.opExtrude","CAP_EDGE",EDGE,{"disambiguationData":[OSD([sQuery(id+"F8.wireOp",EDGE,"E93")])],"isStart":true})});
            var Q4;
            Q4=makeQuery(id+"F9.boolean.opBoolean","COPY",EDGE,{"derivedFrom":makeQuery(id+"F9.opExtrude","CAP_EDGE",EDGE,{"disambiguationData":[OSD([sQuery(id+"F8.wireOp",EDGE,"E95")])],"isStart":true})});
            var Q5;
            Q5=makeQuery(id+"F9.boolean.opBoolean","COPY",EDGE,{"derivedFrom":makeQuery(id+"F9.opExtrude","CAP_EDGE",EDGE,{"disambiguationData":[OSD([sQuery(id+"F8.wireOp",EDGE,"E98.MirrorCS")])],"isStart":true})});
            var Q6;
            Q6=makeQuery(id+"F9.boolean.opBoolean","COPY",EDGE,{"derivedFrom":makeQuery(id+"F9.opExtrude","CAP_EDGE",EDGE,{"disambiguationData":[OSD([sQuery(id+"F8.wireOp",EDGE,"E99.MirrorCS")])],"isStart":true})});
            var Q7;
            Q7=makeQuery(id+"F9.boolean.opBoolean","COPY",EDGE,{"derivedFrom":makeQuery(id+"F9.opExtrude","CAP_EDGE",EDGE,{"disambiguationData":[OSD([sQuery(id+"F8.wireOp",EDGE,"E100.MirrorCS")])],"isStart":true})});
            var Q8;
            Q8=makeQuery(id+"F9.boolean.opBoolean","COPY",EDGE,{"derivedFrom":makeQuery(id+"F9.opExtrude","CAP_EDGE",EDGE,{"disambiguationData":[OSD([sQuery(id+"F8.wireOp",EDGE,"E101.MirrorCS")])],"isStart":true})});
            var Q9;
            Q9=makeQuery(id+"F9.boolean.opBoolean","COPY",EDGE,{"derivedFrom":makeQuery(id+"F9.opExtrude","CAP_EDGE",EDGE,{"disambiguationData":[OSD([sQuery(id+"F8.wireOp",EDGE,"E103.MirrorCS")])],"isStart":true})});
            var Q10;
            Q10=makeQuery(id+"F9.boolean.opBoolean","COPY",EDGE,{"derivedFrom":makeQuery(id+"F9.opExtrude","CAP_EDGE",EDGE,{"disambiguationData":[OSD([sQuery(id+"F8.wireOp",EDGE,"E102.MirrorCS")])],"isStart":true})});
            var Q11;
            Q11=makeQuery(id+"F9.boolean.opBoolean","COPY",EDGE,{"derivedFrom":makeQuery(id+"F9.opExtrude","CAP_EDGE",EDGE,{"disambiguationData":[OSD([sQuery(id+"F8.wireOp",EDGE,"E106.MirrorCS")])],"isStart":true})});
            var Q12;
            Q12=makeQuery(id+"F9.boolean.opBoolean","COPY",EDGE,{"derivedFrom":makeQuery(id+"F9.opExtrude","CAP_EDGE",EDGE,{"disambiguationData":[OSD([sQuery(id+"F8.wireOp",EDGE,"E104.MirrorCS")])],"isStart":true})});
            var Q13;
            Q13=makeQuery(id+"F9.boolean.opBoolean","COPY",EDGE,{"derivedFrom":makeQuery(id+"F9.opExtrude","CAP_EDGE",EDGE,{"disambiguationData":[OSD([sQuery(id+"F8.wireOp",EDGE,"E105.MirrorCS")])],"isStart":true})});
            var Q14;
            Q14=makeQuery(id+"F9.boolean.opBoolean","INTERSECT",EDGE,{"derivedFrom":[makeQuery(id+"F1.opExtrude","CAP_FACE",FACE,{"disambiguationData":[OSD([sQuery(id+"F0.wireOp",EDGE,"E0"),sQuery(id+"F0.wireOp",EDGE,"E1"),sQuery(id+"F0.wireOp",EDGE,"E2"),sQuery(id+"F0.wireOp",EDGE,"E3"),sQuery(id+"F0.wireOp",EDGE,"E6"),sQuery(id+"F0.wireOp",EDGE,"E7"),sQuery(id+"F0.wireOp",EDGE,"E8"),sQuery(id+"F0.wireOp",EDGE,"E9"),sQuery(id+"F0.wireOp",EDGE,"E10"),sQuery(id+"F0.wireOp",EDGE,"E11"),sQuery(id+"F0.wireOp",EDGE,"E12"),sQuery(id+"F0.wireOp",EDGE,"E13"),sQuery(id+"F0.wireOp",EDGE,"E14"),sQuery(id+"F0.wireOp",EDGE,"E15")])],"isStart":true}),makeQuery(id+"F9.opExtrude","SWEPT_FACE",FACE,{"disambiguationData":[OSD([sQuery(id+"F8.wireOp",EDGE,"E106.MirrorCS")])]})]});
            var Q15;
            Q15=makeQuery(id+"F9.boolean.opBoolean","INTERSECT",EDGE,{"derivedFrom":[makeQuery(id+"F1.opExtrude","CAP_FACE",FACE,{"disambiguationData":[OSD([sQuery(id+"F0.wireOp",EDGE,"E0"),sQuery(id+"F0.wireOp",EDGE,"E1"),sQuery(id+"F0.wireOp",EDGE,"E2"),sQuery(id+"F0.wireOp",EDGE,"E3"),sQuery(id+"F0.wireOp",EDGE,"E6"),sQuery(id+"F0.wireOp",EDGE,"E7"),sQuery(id+"F0.wireOp",EDGE,"E8"),sQuery(id+"F0.wireOp",EDGE,"E9"),sQuery(id+"F0.wireOp",EDGE,"E10"),sQuery(id+"F0.wireOp",EDGE,"E11"),sQuery(id+"F0.wireOp",EDGE,"E12"),sQuery(id+"F0.wireOp",EDGE,"E13"),sQuery(id+"F0.wireOp",EDGE,"E14"),sQuery(id+"F0.wireOp",EDGE,"E15")])],"isStart":true}),makeQuery(id+"F9.opExtrude","SWEPT_FACE",FACE,{"disambiguationData":[OSD([sQuery(id+"F8.wireOp",EDGE,"E105.MirrorCS")])]})]});
            var Q16;
            Q16=makeQuery(id+"F9.boolean.opBoolean","INTERSECT",EDGE,{"derivedFrom":[makeQuery(id+"F1.opExtrude","CAP_FACE",FACE,{"disambiguationData":[OSD([sQuery(id+"F0.wireOp",EDGE,"E0"),sQuery(id+"F0.wireOp",EDGE,"E1"),sQuery(id+"F0.wireOp",EDGE,"E2"),sQuery(id+"F0.wireOp",EDGE,"E3"),sQuery(id+"F0.wireOp",EDGE,"E6"),sQuery(id+"F0.wireOp",EDGE,"E7"),sQuery(id+"F0.wireOp",EDGE,"E8"),sQuery(id+"F0.wireOp",EDGE,"E9"),sQuery(id+"F0.wireOp",EDGE,"E10"),sQuery(id+"F0.wireOp",EDGE,"E11"),sQuery(id+"F0.wireOp",EDGE,"E12"),sQuery(id+"F0.wireOp",EDGE,"E13"),sQuery(id+"F0.wireOp",EDGE,"E14"),sQuery(id+"F0.wireOp",EDGE,"E15")])],"isStart":true}),makeQuery(id+"F9.opExtrude","SWEPT_FACE",FACE,{"disambiguationData":[OSD([sQuery(id+"F8.wireOp",EDGE,"E104.MirrorCS")])]})]});
            var Q17;
            Q17=makeQuery(id+"F9.boolean.opBoolean","INTERSECT",EDGE,{"derivedFrom":[makeQuery(id+"F1.opExtrude","CAP_FACE",FACE,{"disambiguationData":[OSD([sQuery(id+"F0.wireOp",EDGE,"E0"),sQuery(id+"F0.wireOp",EDGE,"E1"),sQuery(id+"F0.wireOp",EDGE,"E2"),sQuery(id+"F0.wireOp",EDGE,"E3"),sQuery(id+"F0.wireOp",EDGE,"E6"),sQuery(id+"F0.wireOp",EDGE,"E7"),sQuery(id+"F0.wireOp",EDGE,"E8"),sQuery(id+"F0.wireOp",EDGE,"E9"),sQuery(id+"F0.wireOp",EDGE,"E10"),sQuery(id+"F0.wireOp",EDGE,"E11"),sQuery(id+"F0.wireOp",EDGE,"E12"),sQuery(id+"F0.wireOp",EDGE,"E13"),sQuery(id+"F0.wireOp",EDGE,"E14"),sQuery(id+"F0.wireOp",EDGE,"E15")])],"isStart":true}),makeQuery(id+"F9.opExtrude","SWEPT_FACE",FACE,{"disambiguationData":[OSD([sQuery(id+"F8.wireOp",EDGE,"E93")])]})]});
            var Q18;
            Q18=makeQuery(id+"F9.boolean.opBoolean","INTERSECT",EDGE,{"derivedFrom":[makeQuery(id+"F1.opExtrude","CAP_FACE",FACE,{"disambiguationData":[OSD([sQuery(id+"F0.wireOp",EDGE,"E0"),sQuery(id+"F0.wireOp",EDGE,"E1"),sQuery(id+"F0.wireOp",EDGE,"E2"),sQuery(id+"F0.wireOp",EDGE,"E3"),sQuery(id+"F0.wireOp",EDGE,"E6"),sQuery(id+"F0.wireOp",EDGE,"E7"),sQuery(id+"F0.wireOp",EDGE,"E8"),sQuery(id+"F0.wireOp",EDGE,"E9"),sQuery(id+"F0.wireOp",EDGE,"E10"),sQuery(id+"F0.wireOp",EDGE,"E11"),sQuery(id+"F0.wireOp",EDGE,"E12"),sQuery(id+"F0.wireOp",EDGE,"E13"),sQuery(id+"F0.wireOp",EDGE,"E14"),sQuery(id+"F0.wireOp",EDGE,"E15")])],"isStart":true}),makeQuery(id+"F9.opExtrude","SWEPT_FACE",FACE,{"disambiguationData":[OSD([sQuery(id+"F8.wireOp",EDGE,"E95")])]})]});
            var Q19;
            Q19=makeQuery(id+"F9.boolean.opBoolean","INTERSECT",EDGE,{"derivedFrom":[makeQuery(id+"F1.opExtrude","CAP_FACE",FACE,{"disambiguationData":[OSD([sQuery(id+"F0.wireOp",EDGE,"E0"),sQuery(id+"F0.wireOp",EDGE,"E1"),sQuery(id+"F0.wireOp",EDGE,"E2"),sQuery(id+"F0.wireOp",EDGE,"E3"),sQuery(id+"F0.wireOp",EDGE,"E6"),sQuery(id+"F0.wireOp",EDGE,"E7"),sQuery(id+"F0.wireOp",EDGE,"E8"),sQuery(id+"F0.wireOp",EDGE,"E9"),sQuery(id+"F0.wireOp",EDGE,"E10"),sQuery(id+"F0.wireOp",EDGE,"E11"),sQuery(id+"F0.wireOp",EDGE,"E12"),sQuery(id+"F0.wireOp",EDGE,"E13"),sQuery(id+"F0.wireOp",EDGE,"E14"),sQuery(id+"F0.wireOp",EDGE,"E15")])],"isStart":true}),makeQuery(id+"F9.opExtrude","SWEPT_FACE",FACE,{"disambiguationData":[OSD([sQuery(id+"F8.wireOp",EDGE,"E94")])]})]});
            var Q20;
            Q20=makeQuery(id+"F9.boolean.opBoolean","INTERSECT",EDGE,{"derivedFrom":[makeQuery(id+"F1.opExtrude","CAP_FACE",FACE,{"disambiguationData":[OSD([sQuery(id+"F0.wireOp",EDGE,"E0"),sQuery(id+"F0.wireOp",EDGE,"E1"),sQuery(id+"F0.wireOp",EDGE,"E2"),sQuery(id+"F0.wireOp",EDGE,"E3"),sQuery(id+"F0.wireOp",EDGE,"E6"),sQuery(id+"F0.wireOp",EDGE,"E7"),sQuery(id+"F0.wireOp",EDGE,"E8"),sQuery(id+"F0.wireOp",EDGE,"E9"),sQuery(id+"F0.wireOp",EDGE,"E10"),sQuery(id+"F0.wireOp",EDGE,"E11"),sQuery(id+"F0.wireOp",EDGE,"E12"),sQuery(id+"F0.wireOp",EDGE,"E13"),sQuery(id+"F0.wireOp",EDGE,"E14"),sQuery(id+"F0.wireOp",EDGE,"E15")])],"isStart":true}),makeQuery(id+"F9.opExtrude","SWEPT_FACE",FACE,{"disambiguationData":[OSD([sQuery(id+"F8.wireOp",EDGE,"E103.MirrorCS")])]})]});
            var Q21;
            Q21=makeQuery(id+"F9.boolean.opBoolean","INTERSECT",EDGE,{"derivedFrom":[makeQuery(id+"F1.opExtrude","CAP_FACE",FACE,{"disambiguationData":[OSD([sQuery(id+"F0.wireOp",EDGE,"E0"),sQuery(id+"F0.wireOp",EDGE,"E1"),sQuery(id+"F0.wireOp",EDGE,"E2"),sQuery(id+"F0.wireOp",EDGE,"E3"),sQuery(id+"F0.wireOp",EDGE,"E6"),sQuery(id+"F0.wireOp",EDGE,"E7"),sQuery(id+"F0.wireOp",EDGE,"E8"),sQuery(id+"F0.wireOp",EDGE,"E9"),sQuery(id+"F0.wireOp",EDGE,"E10"),sQuery(id+"F0.wireOp",EDGE,"E11"),sQuery(id+"F0.wireOp",EDGE,"E12"),sQuery(id+"F0.wireOp",EDGE,"E13"),sQuery(id+"F0.wireOp",EDGE,"E14"),sQuery(id+"F0.wireOp",EDGE,"E15")])],"isStart":true}),makeQuery(id+"F9.opExtrude","SWEPT_FACE",FACE,{"disambiguationData":[OSD([sQuery(id+"F8.wireOp",EDGE,"E101.MirrorCS")])]})]});
            var Q22;
            Q22=makeQuery(id+"F9.boolean.opBoolean","INTERSECT",EDGE,{"derivedFrom":[makeQuery(id+"F1.opExtrude","CAP_FACE",FACE,{"disambiguationData":[OSD([sQuery(id+"F0.wireOp",EDGE,"E0"),sQuery(id+"F0.wireOp",EDGE,"E1"),sQuery(id+"F0.wireOp",EDGE,"E2"),sQuery(id+"F0.wireOp",EDGE,"E3"),sQuery(id+"F0.wireOp",EDGE,"E6"),sQuery(id+"F0.wireOp",EDGE,"E7"),sQuery(id+"F0.wireOp",EDGE,"E8"),sQuery(id+"F0.wireOp",EDGE,"E9"),sQuery(id+"F0.wireOp",EDGE,"E10"),sQuery(id+"F0.wireOp",EDGE,"E11"),sQuery(id+"F0.wireOp",EDGE,"E12"),sQuery(id+"F0.wireOp",EDGE,"E13"),sQuery(id+"F0.wireOp",EDGE,"E14"),sQuery(id+"F0.wireOp",EDGE,"E15")])],"isStart":true}),makeQuery(id+"F9.opExtrude","SWEPT_FACE",FACE,{"disambiguationData":[OSD([sQuery(id+"F8.wireOp",EDGE,"E102.MirrorCS")])]})]});
            var Q23;
            Q23=makeQuery(id+"F9.boolean.opBoolean","INTERSECT",EDGE,{"derivedFrom":[makeQuery(id+"F1.opExtrude","CAP_FACE",FACE,{"disambiguationData":[OSD([sQuery(id+"F0.wireOp",EDGE,"E0"),sQuery(id+"F0.wireOp",EDGE,"E1"),sQuery(id+"F0.wireOp",EDGE,"E2"),sQuery(id+"F0.wireOp",EDGE,"E3"),sQuery(id+"F0.wireOp",EDGE,"E6"),sQuery(id+"F0.wireOp",EDGE,"E7"),sQuery(id+"F0.wireOp",EDGE,"E8"),sQuery(id+"F0.wireOp",EDGE,"E9"),sQuery(id+"F0.wireOp",EDGE,"E10"),sQuery(id+"F0.wireOp",EDGE,"E11"),sQuery(id+"F0.wireOp",EDGE,"E12"),sQuery(id+"F0.wireOp",EDGE,"E13"),sQuery(id+"F0.wireOp",EDGE,"E14"),sQuery(id+"F0.wireOp",EDGE,"E15")])],"isStart":true}),makeQuery(id+"F9.opExtrude","SWEPT_FACE",FACE,{"disambiguationData":[OSD([sQuery(id+"F8.wireOp",EDGE,"E99.MirrorCS")])]})]});
            var Q24;
            Q24=makeQuery(id+"F9.boolean.opBoolean","INTERSECT",EDGE,{"derivedFrom":[makeQuery(id+"F1.opExtrude","CAP_FACE",FACE,{"disambiguationData":[OSD([sQuery(id+"F0.wireOp",EDGE,"E0"),sQuery(id+"F0.wireOp",EDGE,"E1"),sQuery(id+"F0.wireOp",EDGE,"E2"),sQuery(id+"F0.wireOp",EDGE,"E3"),sQuery(id+"F0.wireOp",EDGE,"E6"),sQuery(id+"F0.wireOp",EDGE,"E7"),sQuery(id+"F0.wireOp",EDGE,"E8"),sQuery(id+"F0.wireOp",EDGE,"E9"),sQuery(id+"F0.wireOp",EDGE,"E10"),sQuery(id+"F0.wireOp",EDGE,"E11"),sQuery(id+"F0.wireOp",EDGE,"E12"),sQuery(id+"F0.wireOp",EDGE,"E13"),sQuery(id+"F0.wireOp",EDGE,"E14"),sQuery(id+"F0.wireOp",EDGE,"E15")])],"isStart":true}),makeQuery(id+"F9.opExtrude","SWEPT_FACE",FACE,{"disambiguationData":[OSD([sQuery(id+"F8.wireOp",EDGE,"E100.MirrorCS")])]})]});
            var Q25;
            Q25=makeQuery(id+"F9.boolean.opBoolean","INTERSECT",EDGE,{"derivedFrom":[makeQuery(id+"F1.opExtrude","CAP_FACE",FACE,{"disambiguationData":[OSD([sQuery(id+"F0.wireOp",EDGE,"E0"),sQuery(id+"F0.wireOp",EDGE,"E1"),sQuery(id+"F0.wireOp",EDGE,"E2"),sQuery(id+"F0.wireOp",EDGE,"E3"),sQuery(id+"F0.wireOp",EDGE,"E6"),sQuery(id+"F0.wireOp",EDGE,"E7"),sQuery(id+"F0.wireOp",EDGE,"E8"),sQuery(id+"F0.wireOp",EDGE,"E9"),sQuery(id+"F0.wireOp",EDGE,"E10"),sQuery(id+"F0.wireOp",EDGE,"E11"),sQuery(id+"F0.wireOp",EDGE,"E12"),sQuery(id+"F0.wireOp",EDGE,"E13"),sQuery(id+"F0.wireOp",EDGE,"E14"),sQuery(id+"F0.wireOp",EDGE,"E15")])],"isStart":true}),makeQuery(id+"F9.opExtrude","SWEPT_FACE",FACE,{"disambiguationData":[OSD([sQuery(id+"F8.wireOp",EDGE,"E98.MirrorCS")])]})]});
            chamfer(context, id + "F10", {"entities" : qUnion([Q0, Q1, Q2, Q3, Q4, Q5, Q6, Q7, Q8, Q9, Q10, Q11, Q12, Q13, Q14, Q15, Q16, Q17, Q18, Q19, Q20, Q21, Q22, Q23, Q24, Q25]), "width" : 0.4 * mm, "tangentPropagation" : true});
        }
    });
